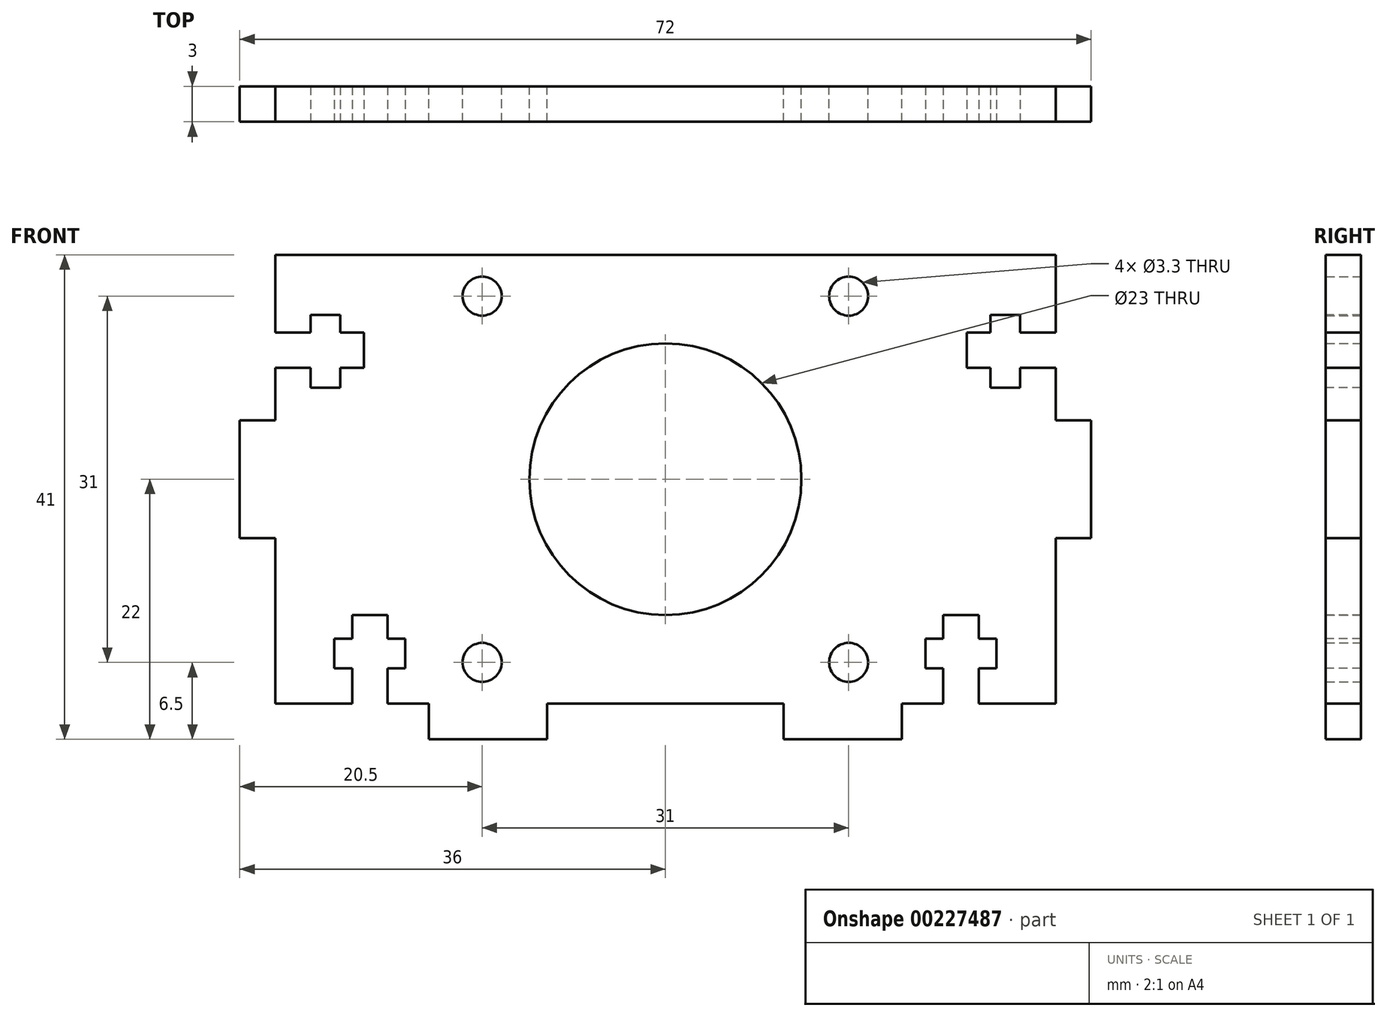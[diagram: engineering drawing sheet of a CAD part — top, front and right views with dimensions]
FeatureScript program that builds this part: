
annotation { "Feature Type Name" : "Feature", "Feature Type Description" : "" }
export const myFeature = defineFeature(function(context is Context, id is Id, definition is map)
    precondition{}
    {
        {
            var Q0;
            Q0=qCreatedBy(makeId("Front.planeOp"),FACE);
            var sketch = newSketch(context, id + "F0", { "sketchPlane" : qUnion([Q0])});
            skLineSegment(sketch, "E0.top", {"start": v(33, 19) * mm, "end": v(-33, 19) * mm});
            skPoint(sketch, "E0.middle", {"position": v(0, 0) * mm});
            skCircle(sketch, "E1", {"center": v(0, 0) * mm, "radius": 11.5 * mm});
            skPoint(sketch, "E2", {"position": v(0, 19) * mm});
            skLineSegment(sketch, "E3", {"start": v(-20, -19) * mm, "end": v(-20, -22) * mm});
            skLineSegment(sketch, "E4", {"start": v(-20, -22) * mm, "end": v(-10, -22) * mm});
            skLineSegment(sketch, "E5", {"start": v(-10, -22) * mm, "end": v(-10, -19) * mm});
            skLineSegment(sketch, "E6", {"start": v(-10, -19) * mm, "end": v(0, -19) * mm});
            skLineSegment(sketch, "E7.MirrorCS", {"start": v(10, -19) * mm, "end": v(0, -19) * mm});
            skLineSegment(sketch, "E8.MirrorCS", {"start": v(10, -22) * mm, "end": v(10, -19) * mm});
            skLineSegment(sketch, "E9.MirrorCS", {"start": v(20, -22) * mm, "end": v(10, -22) * mm});
            skLineSegment(sketch, "E10.MirrorCS", {"start": v(20, -19) * mm, "end": v(20, -22) * mm});
            skPoint(sketch, "E11", {"position": v(-15.5, 15.5) * mm});
            skCircle(sketch, "E12", {"center": v(-15.5, 15.5) * mm, "radius": 1.65 * mm});
            skCircle(sketch, "E13.MirrorC", {"center": v(15.5, 15.5) * mm, "radius": 1.65 * mm});
            skCircle(sketch, "E14.MirrorC", {"center": v(-15.5, -15.5) * mm, "radius": 1.65 * mm});
            skCircle(sketch, "E15.MirrorC", {"center": v(15.5, -15.5) * mm, "radius": 1.65 * mm});
            skLineSegment(sketch, "E16", {"start": v(20, -19) * mm, "end": v(33, -19) * mm});
            skLineSegment(sketch, "E17", {"start": v(-20, -19) * mm, "end": v(-33, -19) * mm});
            skLineSegment(sketch, "E18", {"start": v(-33, -19) * mm, "end": v(-33, -5) * mm});
            skLineSegment(sketch, "E19", {"start": v(-33, -5) * mm, "end": v(-36, -5) * mm});
            skLineSegment(sketch, "E20", {"start": v(-36, -5) * mm, "end": v(-36, 5) * mm});
            skLineSegment(sketch, "E21", {"start": v(-36, 5) * mm, "end": v(-33, 5) * mm});
            skLineSegment(sketch, "E22", {"start": v(-33, 5) * mm, "end": v(-33, 19) * mm});
            skPoint(sketch, "E23", {"position": v(-36, 0) * mm});
            skLineSegment(sketch, "E24.MirrorCS", {"start": v(33, -19) * mm, "end": v(33, -5) * mm});
            skLineSegment(sketch, "E25.MirrorCS", {"start": v(33, -5) * mm, "end": v(36, -5) * mm});
            skLineSegment(sketch, "E26.MirrorCS", {"start": v(36, -5) * mm, "end": v(36, 5) * mm});
            skLineSegment(sketch, "E27.MirrorCS", {"start": v(36, 5) * mm, "end": v(33, 5) * mm});
            skLineSegment(sketch, "E28.MirrorCS", {"start": v(33, 5) * mm, "end": v(33, 19) * mm});
            skSolve(sketch);
        }
        {
            var Q0;
            Q0=makeQuery(id+"F0.imprint","IMPRINT",FACE,{"disambiguationData":[TD([[makeQuery(id+"F0.imprint","IMPRINT",EDGE,{"derivedFrom":sQuery(id+"F0.wireOp",EDGE,"E0.bottom")}),-1.0]])]});
            var Q1;
            Q1=makeQuery(id+"F0.imprint","IMPRINT",FACE,{"disambiguationData":[TD([[makeQuery(id+"F0.imprint","IMPRINT",EDGE,{"derivedFrom":sQuery(id+"F0.wireOp",EDGE,"E0.top")}),1.0]])]});
            extrude(context, id + "F1", {"entities" : qUnion([Q0, Q1]), "depth" : 3 * mm});
        }
        {
            var Q0;
            Q0=makeQuery(id+"F1.opExtrude","CAP_FACE",FACE,{"disambiguationData":[OSD([sQuery(id+"F0.wireOp",EDGE,"E0.top"),sQuery(id+"F0.wireOp",EDGE,"E0.left"),sQuery(id+"F0.wireOp",EDGE,"E0.right"),sQuery(id+"F0.wireOp",EDGE,"E1"),sQuery(id+"F0.wireOp",EDGE,"i2BJ4We7-Z1tz-6YYD-7Gnh-UwGsJDHukj4o"),sQuery(id+"F0.wireOp",EDGE,"H5TLaSxA-TAvm-WxYI-6s5p-rbUKsHJPtpz8"),sQuery(id+"F0.wireOp",EDGE,"fE5sAuBm-J1N4-LUQK-MxoP-oJGd3h4EWBky"),sQuery(id+"F0.wireOp",EDGE,"UVkaeSOW-HMeC-MlRq-fWxO-58zO0Vm4gzLd"),sQuery(id+"F0.wireOp",EDGE,"4oAcHBtJ-SWL1-Us38-5a5N-tiTYXxMsnVxl"),sQuery(id+"F0.wireOp",EDGE,"MGHFterx-abw6-INuc-nvHV-QaNsLm6ah1ng"),sQuery(id+"F0.wireOp",EDGE,"DztduCwT-NtgE-rZnK-mSEW-EnSqVKOmk10X"),sQuery(id+"F0.wireOp",EDGE,"XImseshz-UxQT-ogDy-5Lvy-O5B2oz8zv5fS"),sQuery(id+"F0.wireOp",EDGE,"FHz1HeJZ-Y50a-yfiC-Rnzm-b0fU7RSFoIpM"),sQuery(id+"F0.wireOp",EDGE,"bBcTDBjg-FDSx-XcTB-SbE1-9syf6QqrHLmC"),sQuery(id+"F0.wireOp",EDGE,"1vXtDNT1-yAZY-NYDk-InIM-wFA5S2rVquaF"),sQuery(id+"F0.wireOp",EDGE,"rcTIoJpC-EadT-N3WT-61kg-b3dVzh2UPf16"),sQuery(id+"F0.wireOp",EDGE,"V9EOst0m-YofT-ZeQ4-KXmd-etc1AHxpQRv2"),sQuery(id+"F0.wireOp",EDGE,"E3"),sQuery(id+"F0.wireOp",EDGE,"E4"),sQuery(id+"F0.wireOp",EDGE,"E5"),sQuery(id+"F0.wireOp",EDGE,"E6"),sQuery(id+"F0.wireOp",EDGE,"E7.MirrorCS"),sQuery(id+"F0.wireOp",EDGE,"E8.MirrorCS"),sQuery(id+"F0.wireOp",EDGE,"E9.MirrorCS"),sQuery(id+"F0.wireOp",EDGE,"E10.MirrorCS"),sQuery(id+"F0.wireOp",EDGE,"4fc586d0-1a2d-4033-9ad1-b4b14924f1e60.MirrorCS"),sQuery(id+"F0.wireOp",EDGE,"25921314-2feb-4960-9358-c6f40c29e8060.MirrorCS"),sQuery(id+"F0.wireOp",EDGE,"92609e8c-4cca-44cb-b192-d1e8ea80d6400.MirrorCS"),sQuery(id+"F0.wireOp",EDGE,"c6435143-3ef5-4a16-a53c-0c7a1f294e250.MirrorCS"),sQuery(id+"F0.wireOp",EDGE,"302a1fd6-7f51-4dcd-b85b-b87c70c5ff6f0.MirrorCS"),sQuery(id+"F0.wireOp",EDGE,"271ff51f-9e70-48b1-9ca4-6ffa4ba6ee090.MirrorCS"),sQuery(id+"F0.wireOp",EDGE,"7c8ad784-0027-4aca-88da-cb9512f49f770.MirrorCS"),sQuery(id+"F0.wireOp",EDGE,"aab8c399-5e78-4643-9a76-05bc1427fb740.MirrorCS"),sQuery(id+"F0.wireOp",EDGE,"2a5f69ab-9c37-4cf4-a27a-83d52b59f34f0.MirrorCS"),sQuery(id+"F0.wireOp",EDGE,"8a72d888-9ff6-4074-9ea7-52382edc54d80.MirrorCS"),sQuery(id+"F0.wireOp",EDGE,"2b144515-558f-4b7e-bfd9-8a7150f656b50.MirrorCS"),sQuery(id+"F0.wireOp",EDGE,"7271def4-b984-4847-8607-e135956054630.MirrorCS"),sQuery(id+"F0.wireOp",EDGE,"d1406031-9f0b-476a-854e-e83de3dd73970.MirrorCS"),sQuery(id+"F0.wireOp",EDGE,"E12"),sQuery(id+"F0.wireOp",EDGE,"E13.MirrorC"),sQuery(id+"F0.wireOp",EDGE,"E14.MirrorC"),sQuery(id+"F0.wireOp",EDGE,"E15.MirrorC")])],"isStart":false});
            var sketch = newSketch(context, id + "F2", { "sketchPlane" : qUnion([Q0])});
            skLineSegment(sketch, "E29", {"start": v(23.5, -19) * mm, "end": v(23.5, -16) * mm});
            skLineSegment(sketch, "E30", {"start": v(23.5, -16) * mm, "end": v(22, -16) * mm});
            skLineSegment(sketch, "E31", {"start": v(22, -16) * mm, "end": v(22, -13.5) * mm});
            skLineSegment(sketch, "E32", {"start": v(22, -13.5) * mm, "end": v(23.5, -13.5) * mm});
            skLineSegment(sketch, "E33", {"start": v(23.5, -13.5) * mm, "end": v(23.5, -11.5) * mm});
            skLineSegment(sketch, "E34", {"start": v(23.5, -11.5) * mm, "end": v(26.5, -11.5) * mm});
            skLineSegment(sketch, "E35", {"start": v(26.5, -11.5) * mm, "end": v(26.5, -13.5) * mm});
            skLineSegment(sketch, "E36", {"start": v(26.5, -13.5) * mm, "end": v(28, -13.5) * mm});
            skLineSegment(sketch, "E37", {"start": v(28, -13.5) * mm, "end": v(28, -16) * mm});
            skLineSegment(sketch, "E38", {"start": v(28, -16) * mm, "end": v(26.5, -16) * mm});
            skLineSegment(sketch, "E39", {"start": v(26.5, -16) * mm, "end": v(26.5, -19) * mm});
            skPoint(sketch, "E40", {"position": v(25, -19) * mm});
            skLineSegment(sketch, "E41", {"start": v(26.5, -19) * mm, "end": v(23.5, -19) * mm});
            skLineSegment(sketch, "E42.MirrorCS", {"start": v(-22, -13.5) * mm, "end": v(-23.5, -13.5) * mm});
            skLineSegment(sketch, "E43.MirrorCS", {"start": v(-23.5, -16) * mm, "end": v(-22, -16) * mm});
            skLineSegment(sketch, "E44.MirrorCS", {"start": v(-28, -16) * mm, "end": v(-26.5, -16) * mm});
            skLineSegment(sketch, "E45.MirrorCS", {"start": v(-26.5, -13.5) * mm, "end": v(-28, -13.5) * mm});
            skLineSegment(sketch, "E46.MirrorCS", {"start": v(-26.5, -11.5) * mm, "end": v(-26.5, -13.5) * mm});
            skLineSegment(sketch, "E47.MirrorCS", {"start": v(-23.5, -13.5) * mm, "end": v(-23.5, -11.5) * mm});
            skLineSegment(sketch, "E48.MirrorCS", {"start": v(-26.5, -19) * mm, "end": v(-23.5, -19) * mm});
            skLineSegment(sketch, "E49.MirrorCS", {"start": v(-22, -16) * mm, "end": v(-22, -13.5) * mm});
            skLineSegment(sketch, "E50.MirrorCS", {"start": v(-23.5, -11.5) * mm, "end": v(-26.5, -11.5) * mm});
            skLineSegment(sketch, "E51.MirrorCS", {"start": v(-26.5, -16) * mm, "end": v(-26.5, -19) * mm});
            skLineSegment(sketch, "E52.MirrorCS", {"start": v(-23.5, -19) * mm, "end": v(-23.5, -16) * mm});
            skLineSegment(sketch, "E53.MirrorCS", {"start": v(-28, -13.5) * mm, "end": v(-28, -16) * mm});
            skPoint(sketch, "E54.MirrorP", {"position": v(-25, -19) * mm});
            skPoint(sketch, "E55", {"position": v(33, 11) * mm});
            skLineSegment(sketch, "E56", {"start": v(33, 11) * mm, "end": v(33, 9.42) * mm});
            skLineSegment(sketch, "E57", {"start": v(33, 9.42) * mm, "end": v(30, 9.42) * mm});
            skLineSegment(sketch, "E58", {"start": v(30, 9.42) * mm, "end": v(30, 7.73) * mm});
            skLineSegment(sketch, "E59", {"start": v(30, 7.73) * mm, "end": v(27.5, 7.73) * mm});
            skLineSegment(sketch, "E60", {"start": v(27.5, 7.73) * mm, "end": v(27.5, 9.42) * mm});
            skLineSegment(sketch, "E61", {"start": v(27.5, 9.42) * mm, "end": v(25.5, 9.42) * mm});
            skLineSegment(sketch, "E62", {"start": v(25.5, 9.42) * mm, "end": v(25.5, 12.42) * mm});
            skLineSegment(sketch, "E63", {"start": v(25.5, 12.42) * mm, "end": v(27.5, 12.42) * mm});
            skLineSegment(sketch, "E64", {"start": v(27.5, 12.42) * mm, "end": v(27.5, 13.92) * mm});
            skLineSegment(sketch, "E65", {"start": v(27.5, 13.92) * mm, "end": v(30, 13.92) * mm});
            skLineSegment(sketch, "E66", {"start": v(30, 13.92) * mm, "end": v(30, 12.42) * mm});
            skLineSegment(sketch, "E67", {"start": v(30, 12.42) * mm, "end": v(33, 12.42) * mm});
            skLineSegment(sketch, "E68", {"start": v(33, 12.42) * mm, "end": v(33, 11) * mm});
            skLineSegment(sketch, "E69.MirrorCS", {"start": v(-25.5, 12.42) * mm, "end": v(-27.5, 12.42) * mm});
            skLineSegment(sketch, "E70.MirrorCS", {"start": v(-33, 12.42) * mm, "end": v(-33, 11) * mm});
            skLineSegment(sketch, "E71.MirrorCS", {"start": v(-27.5, 12.42) * mm, "end": v(-27.5, 13.92) * mm});
            skLineSegment(sketch, "E72.MirrorCS", {"start": v(-27.5, 7.73) * mm, "end": v(-27.5, 9.42) * mm});
            skLineSegment(sketch, "E73.MirrorCS", {"start": v(-30, 7.73) * mm, "end": v(-27.5, 7.73) * mm});
            skLineSegment(sketch, "E74.MirrorCS", {"start": v(-25.5, 9.42) * mm, "end": v(-25.5, 12.42) * mm});
            skLineSegment(sketch, "E75.MirrorCS", {"start": v(-30, 13.92) * mm, "end": v(-30, 12.42) * mm});
            skLineSegment(sketch, "E76.MirrorCS", {"start": v(-27.5, 9.42) * mm, "end": v(-25.5, 9.42) * mm});
            skLineSegment(sketch, "E77.MirrorCS", {"start": v(-33, 11) * mm, "end": v(-33, 9.42) * mm});
            skPoint(sketch, "E78.MirrorP", {"position": v(-33, 11) * mm});
            skLineSegment(sketch, "E79.MirrorCS", {"start": v(-30, 9.42) * mm, "end": v(-30, 7.73) * mm});
            skLineSegment(sketch, "E80.MirrorCS", {"start": v(-27.5, 13.92) * mm, "end": v(-30, 13.92) * mm});
            skLineSegment(sketch, "E81.MirrorCS", {"start": v(-30, 12.42) * mm, "end": v(-33, 12.42) * mm});
            skLineSegment(sketch, "E82.MirrorCS", {"start": v(-33, 9.42) * mm, "end": v(-30, 9.42) * mm});
            skSolve(sketch);
        }
        {
            var Q0;
            Q0=makeQuery(id+"F2.imprint","IMPRINT",FACE,{"disambiguationData":[TD([[makeQuery(id+"F2.imprint","IMPRINT",EDGE,{"derivedFrom":sQuery(id+"F2.wireOp",EDGE,"E29")}),-1.0]])]});
            var Q1;
            Q1=makeQuery(id+"F2.imprint","IMPRINT",FACE,{"disambiguationData":[TD([[makeQuery(id+"F2.imprint","IMPRINT",EDGE,{"derivedFrom":sQuery(id+"F2.wireOp",EDGE,"E42.MirrorCS")}),1.0]])]});
            var Q2;
            Q2=makeQuery(id+"F2.imprint","IMPRINT",FACE,{"disambiguationData":[TD([[makeQuery(id+"F2.imprint","IMPRINT",EDGE,{"derivedFrom":sQuery(id+"F2.wireOp",EDGE,"E56")}),1.0]])]});
            var Q3;
            Q3=makeQuery(id+"F2.imprint","IMPRINT",FACE,{"disambiguationData":[TD([[makeQuery(id+"F2.imprint","IMPRINT",EDGE,{"derivedFrom":sQuery(id+"F2.wireOp",EDGE,"E69.MirrorCS")}),1.0]])]});
            extrude(context, id + "F3", {"entities" : qUnion([Q0, Q1, Q2, Q3]), "operationType" : NewBodyOperationType.REMOVE, "endBound" : BoundingType.UP_TO_NEXT, "oppositeDirection" : true, "depth" : 25 * mm});
        }
    });
